# Revit family: Shower-Valve_Trim-KOHLER-Aleo-K-72290IN
name_source: partatom
category: Specialty Equipment
revit_build: Autodesk Revit 2017 (Build: 20160225_1515(x64)
units: mm (PartAtom-declared; Revit-internal decimal feet)

## family parameters
Cut with Voids When Loaded = No
Host = Face
OmniClass Number = 23.31.25.00
Part Type = Normal
Room Calculation Point = No
Round Connector Dimension = Use Diameter
Shared = No

## types (6) — shared parameters
ADA Compliant = No
Assembly Code = C1030200
Date Modified = 10/08/2020
Default Elevation = 42"
Height = 6 9/16"
Length = 3 3/16"
Manufacturer = KOHLER Co.
Master Format 2014 = 10 28 00
Master Format 2014 Name = Toilet, Bath, and Laundry Accessories
Material = Metal consrtuction
Product Documentation Link = http://resources.kohler.com
Product Name = Aleo
URL = https://www.kohler.co.in
WaterSense Certified = No
Width = 4 7/16"

## per-type parameters (varying)
| type | Description | Finish | Model | Product Page URL | Type |
| 4, CP- Polished chrome | Recessed Bath & Shower Trim, 40 mm | Kohler-Metal-CP-Polished_Chrome | K-72290IN-4-CP |  | 1 |
| 4, BV- Brushed bronze | Recessed Bath & Shower Trim, 40 mm | Kohler-Metal-BV-Brushed_Bronze | K-72290IN-4-BV | https://www.kohler.co.in | 2 |
| 4, RGD- Polished rose gold | Recessed Bath & Shower Trim, 40 mm | Kohler-Metal-RGD-Polished_Rose_Gold | K-72290IN-4-RGD | https://www.kohler.co.in | 3 |
| 4FP, CP-Polished chrome | Recessed bath and shower trim | Kohler-Metal-CP-Polished_Chrome | K-72290IN-4FP-CP | https://www.kohler.co.in | 4 |
| 4FP, BV-Brushed bronze | Recessed bath and shower trim | Kohler-Metal-BV-Brushed_Bronze | K-72290IN-4FP-BV |  | 5 |
| 4FP, RGD- Polished rose gold | Recessed bath and shower trim | Kohler-Metal-RGD-Polished_Rose_Gold | K-72290IN-4FP-RGD |  | 6 |

## geometry (parser evidence)
native form markers: Sweep x6
no freeform markers — native parametric forms only
